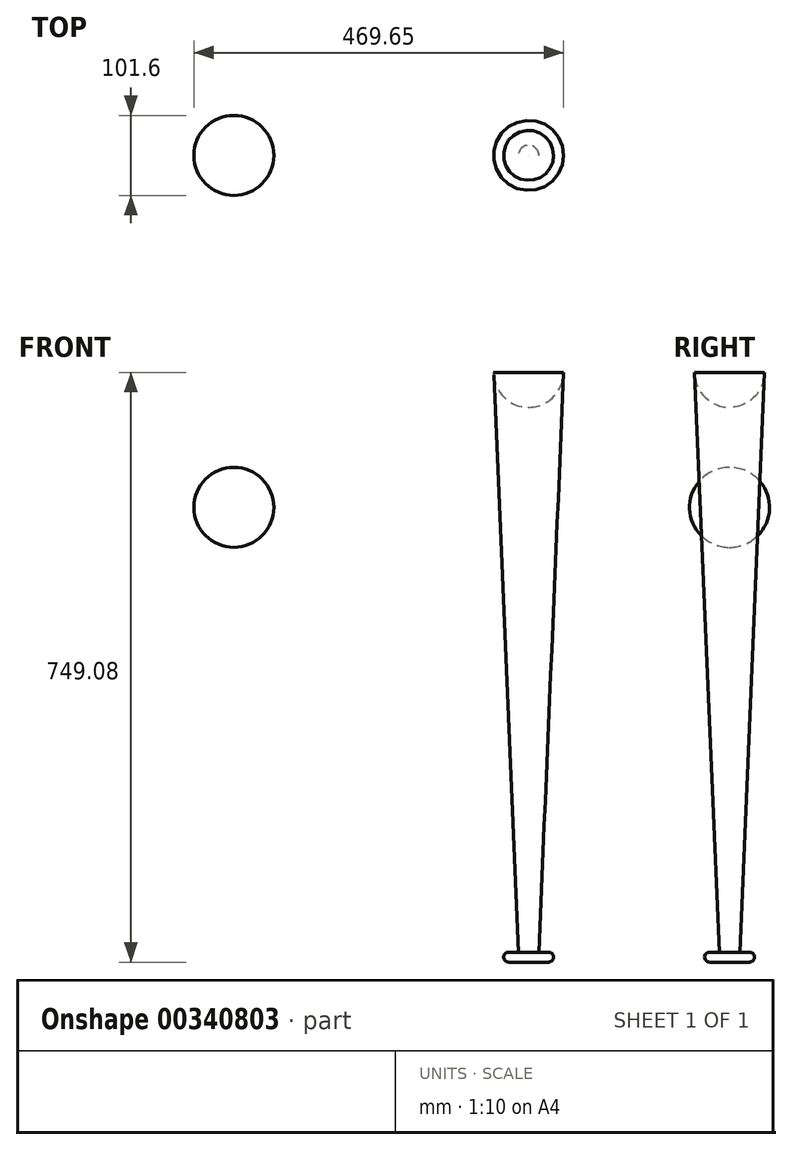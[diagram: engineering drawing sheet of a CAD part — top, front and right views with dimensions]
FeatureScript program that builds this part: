
annotation { "Feature Type Name" : "Feature", "Feature Type Description" : "" }
export const myFeature = defineFeature(function(context is Context, id is Id, definition is map)
    precondition{}
    {
        {
            var Q0;
            Q0=qCreatedBy(makeId("Front.planeOp"),FACE);
            var sketch = newSketch(context, id + "F0", { "sketchPlane" : qUnion([Q0])});
            skLineSegment(sketch, "E0", {"start": v(0, 0) * mm, "end": v(31.48, -736.6) * mm});
            skLineSegment(sketch, "E1", {"start": v(88.92, 0) * mm, "end": v(57.42, -736.6) * mm});
            skArc(sketch, "E2", {"start": v(88.76, -3.58) * mm, "mid": v(44.46, 44.45) * mm, "end": v(0.15, -3.57) * mm});
            skLineSegment(sketch, "E3", {"start": v(44.46, 44.45) * mm, "end": v(44.45, -742.95) * mm});
            skArc(sketch, "E4", {"start": v(19.05, -736.6) * mm, "mid": v(12.7, -742.95) * mm, "end": v(19.05, -749.3) * mm});
            skArc(sketch, "E5", {"start": v(69.85, -749.3) * mm, "mid": v(76.2, -742.95) * mm, "end": v(69.85, -736.6) * mm});
            skLineSegment(sketch, "E6", {"start": v(19.05, -736.6) * mm, "end": v(69.85, -736.6) * mm});
            skLineSegment(sketch, "E7", {"start": v(19.05, -749.3) * mm, "end": v(69.85, -749.3) * mm});
            skLineSegment(sketch, "E8", {"start": v(44.45, -736.6) * mm, "end": v(44.45, -749.3) * mm});
            skPoint(sketch, "E9.orphan", {"position": v(31.75, -742.95) * mm});
            skPoint(sketch, "E10.orphan", {"position": v(57.15, -742.95) * mm});
            skSolve(sketch);
        }
        {
            var Q0;
            {var subQ1=sQuery(id+"F0.wireOp",EDGE,"E2");var subQ3=sQuery(id+"F0.wireOp",EDGE,"E0");var subQ5=makeQuery(id+"F0.imprint","INTERSECT",VERTEX,{"disambiguationData":[OD(0.0)],"derivedFrom":[subQ3,subQ1]});Q0=makeQuery(id+"F0.imprint","IMPRINT",FACE,{"disambiguationData":[TD([[makeQuery(id+"F0.imprint","IMPRINT",EDGE,{"disambiguationData":[TD([[subQ5,1.0]])],"derivedFrom":subQ3}),1.0]])]});}
            var Q1;
            Q1=sQuery(id+"F0.wireOp",EDGE,"E3");
            revolve(context, id + "F1", {"entities" : qUnion([Q0]), "axis" : qUnion([Q1]), "revolveType" : RevolveType.FULL});
        }
        {
            var Q0;
            {var subQ1=sQuery(id+"F0.wireOp",EDGE,"E4");Q0=makeQuery(id+"F0.imprint","IMPRINT",FACE,{"disambiguationData":[TD([[makeQuery(id+"F0.imprint","IMPRINT",EDGE,{"derivedFrom":subQ1}),1.0]])]});}
            var Q1;
            Q1=sQuery(id+"F0.wireOp",EDGE,"E8");
            revolve(context, id + "F2", {"entities" : qUnion([Q0]), "axis" : qUnion([Q1]), "revolveType" : RevolveType.FULL});
        }
        {
            var Q0;
            Q0=qCreatedBy(makeId("Front.planeOp"),FACE);
            var sketch = newSketch(context, id + "F3", { "sketchPlane" : qUnion([Q0])});
            skCircle(sketch, "E11", {"center": v(-329.94, -171.56) * mm, "radius": 50.8 * mm});
            skLineSegment(sketch, "E12", {"start": v(-329.94, -120.76) * mm, "end": v(-329.94, -222.36) * mm});
            skSolve(sketch);
        }
        {
            var Q0;
            {var subQ0=sQuery(id+"F3.wireOp",EDGE,"E12");Q0=makeQuery(id+"F3.imprint","IMPRINT",FACE,{"disambiguationData":[TD([[makeQuery(id+"F3.imprint","IMPRINT",EDGE,{"derivedFrom":subQ0}),-1.0]])]});}
            var Q1;
            Q1=sQuery(id+"F3.wireOp",EDGE,"E12");
            revolve(context, id + "F4", {"entities" : qUnion([Q0]), "axis" : qUnion([Q1]), "revolveType" : RevolveType.FULL});
        }
    });
